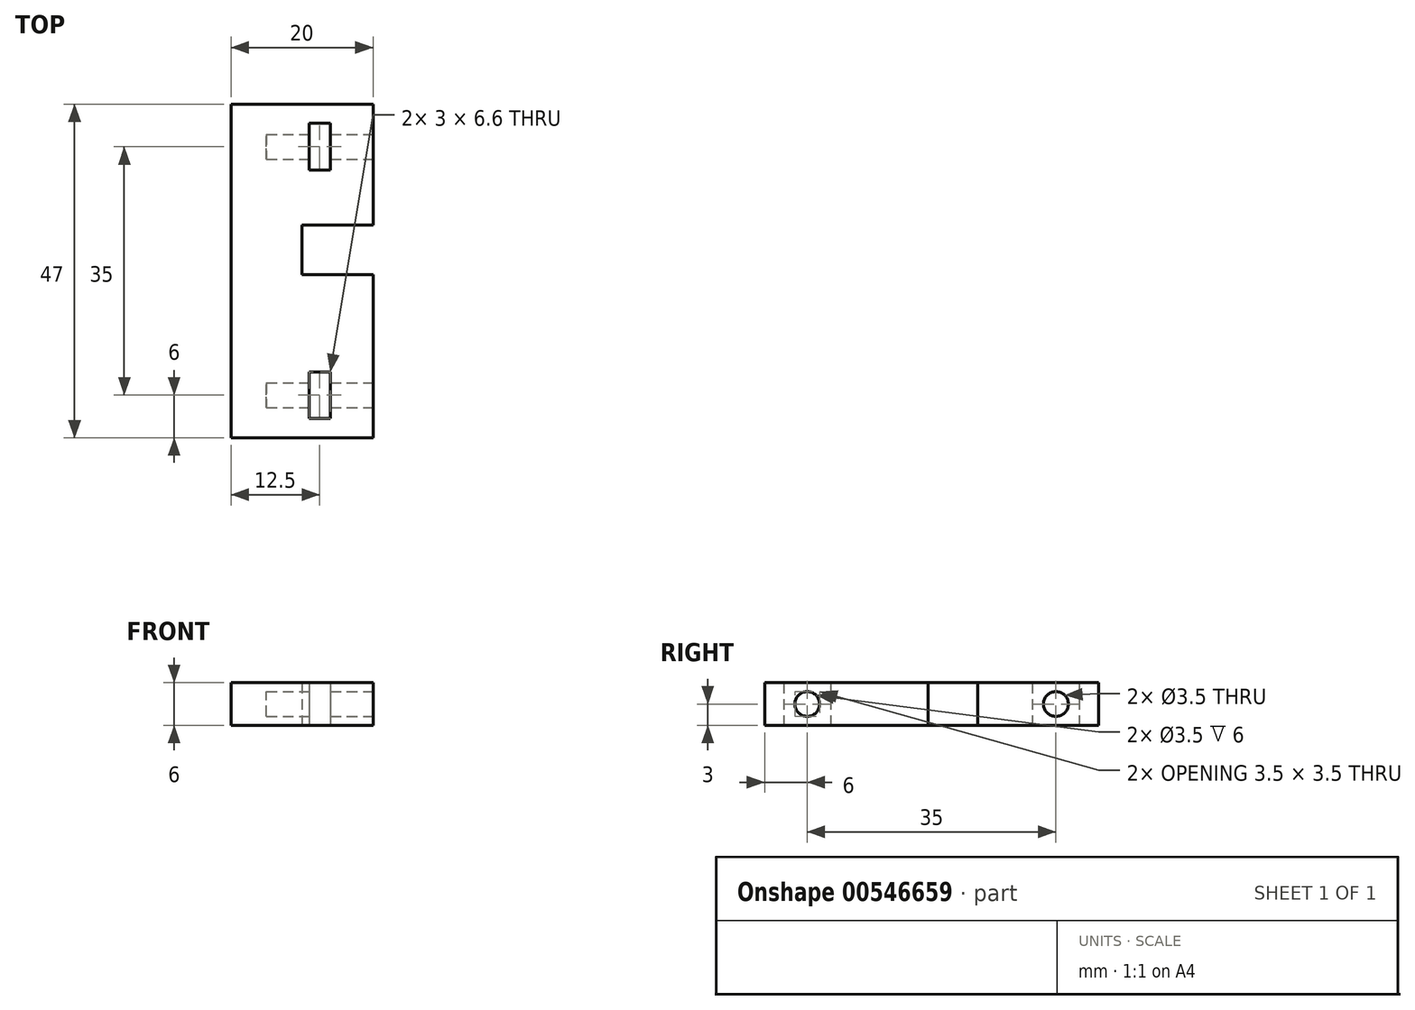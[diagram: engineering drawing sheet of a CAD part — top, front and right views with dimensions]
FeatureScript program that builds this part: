
annotation { "Feature Type Name" : "Feature", "Feature Type Description" : "" }
export const myFeature = defineFeature(function(context is Context, id is Id, definition is map)
    precondition{}
    {
        {
            var Q0;
            Q0=qCreatedBy(makeId("Top.planeOp"),FACE);
            var sketch = newSketch(context, id + "F0", { "sketchPlane" : qUnion([Q0])});
            skLineSegment(sketch, "E0.bottom", {"start": v(0, 0) * mm, "end": v(20, 0) * mm});
            skLineSegment(sketch, "E0.top", {"start": v(0, 47) * mm, "end": v(20, 47) * mm});
            skLineSegment(sketch, "E0.left", {"start": v(0, 0) * mm, "end": v(0, 47) * mm});
            skLineSegment(sketch, "E0.right", {"start": v(20, 0) * mm, "end": v(20, 47) * mm});
            skLineSegment(sketch, "E1.bottom", {"start": v(11, 2.7) * mm, "end": v(14, 2.7) * mm});
            skLineSegment(sketch, "E1.top", {"start": v(11, 9.3) * mm, "end": v(14, 9.3) * mm});
            skLineSegment(sketch, "E1.left", {"start": v(11, 2.7) * mm, "end": v(11, 9.3) * mm});
            skLineSegment(sketch, "E1.right", {"start": v(14, 2.7) * mm, "end": v(14, 9.3) * mm});
            skLineSegment(sketch, "E2.bottom", {"start": v(11, 37.7) * mm, "end": v(14, 37.7) * mm});
            skLineSegment(sketch, "E2.top", {"start": v(11, 44.3) * mm, "end": v(14, 44.3) * mm});
            skLineSegment(sketch, "E2.left", {"start": v(11, 37.7) * mm, "end": v(11, 44.3) * mm});
            skLineSegment(sketch, "E2.right", {"start": v(14, 37.7) * mm, "end": v(14, 44.3) * mm});
            skLineSegment(sketch, "E3.bottom", {"start": v(20, 23) * mm, "end": v(10, 23) * mm});
            skLineSegment(sketch, "E3.top", {"start": v(20, 30) * mm, "end": v(10, 30) * mm});
            skLineSegment(sketch, "E3.left", {"start": v(20, 23) * mm, "end": v(20, 30) * mm});
            skLineSegment(sketch, "E3.right", {"start": v(10, 23) * mm, "end": v(10, 30) * mm});
            skSolve(sketch);
        }
        {
            var Q0;
            Q0=makeQuery(id+"F0.imprint","IMPRINT",FACE,{"disambiguationData":[TD([[makeQuery(id+"F0.imprint","IMPRINT",EDGE,{"derivedFrom":sQuery(id+"F0.wireOp",EDGE,"E0.bottom")}),1.0]])]});
            extrude(context, id + "F1", {"entities" : qUnion([Q0]), "depth" : 6 * mm, "offsetDistance" : 25 * mm});
        }
        {
            var Q0;
            Q0=makeQuery(id+"F1.opExtrude","SWEPT_FACE",FACE,{"disambiguationData":[OSD([sQuery(id+"F0.wireOp",EDGE,"E0.right")])]});
            var sketch = newSketch(context, id + "F2", { "sketchPlane" : qUnion([Q0])});
            skCircle(sketch, "E4", {"center": v(6, 3) * mm, "radius": 1.75 * mm});
            skCircle(sketch, "E5", {"center": v(41, 3) * mm, "radius": 1.75 * mm});
            skSolve(sketch);
        }
        {
            var Q0;
            Q0=makeQuery(id+"F2.imprint","IMPRINT",FACE,{"disambiguationData":[TD([[makeQuery(id+"F2.imprint","IMPRINT",EDGE,{"derivedFrom":sQuery(id+"F2.wireOp",EDGE,"E5")}),1.0]])]});
            var Q1;
            Q1=makeQuery(id+"F2.imprint","IMPRINT",FACE,{"disambiguationData":[TD([[makeQuery(id+"F2.imprint","IMPRINT",EDGE,{"derivedFrom":sQuery(id+"F2.wireOp",EDGE,"E4")}),1.0]])]});
            extrude(context, id + "F3", {"entities" : qUnion([Q0, Q1]), "operationType" : NewBodyOperationType.REMOVE, "oppositeDirection" : true, "depth" : 15 * mm, "offsetDistance" : 25 * mm});
        }
    });
